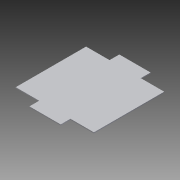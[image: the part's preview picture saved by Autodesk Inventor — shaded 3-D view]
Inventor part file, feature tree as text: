
AUTODESK INVENTOR PART (.ipt)
format: ipt  version: 2014 SP1 (Build 180222100, 222)  size: 93,184 bytes
history: native  units: in
note: dims shown in document units (in); Inventor stores cm internally (conversion verified against a paired STEP export)
features: extrude x2, sketch x2
ambient origin geometry x8: Origin, YZ Plane, XZ Plane, XY Plane, X Axis, Y Axis, Z Axis, Center Point
bodies: Solid1 (feature_tree)
feature tree (4):
  extrude  "Extrusion1"  Depth=23.0in
  extrude  "Extrusion2"  Depth=6.0in
  sketch  "Sketch1"  dims[d0=20.0in d1=23.0in]
  sketch  "Sketch2"  dims[d2=0.25in d3=0.0in d4=6.0in d5=2.5in d6=6.0in d7=2.5in d8=6.0in d9=2.5in d10=6.0in d11=2.5in d12=1.0in d13=0.0in]
